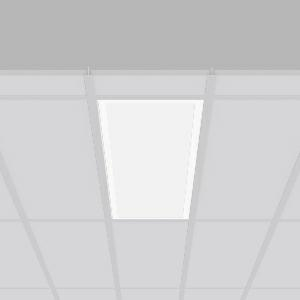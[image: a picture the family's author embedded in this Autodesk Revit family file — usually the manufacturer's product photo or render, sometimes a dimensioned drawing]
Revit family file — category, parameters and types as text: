
# Revit family: sidelite_eco_672377_002_1_5599
name_source: partatom
category: Lighting Fixtures
units: mm (PartAtom-declared; Revit-internal decimal feet)

## family parameters
Cut with Voids When Loaded = No
Host = Face
Light Source = No
Part Type = Normal
Room Calculation Point = No
Round Connector Dimension = Use Diameter
Shared = No

## types (1)
- SIDELITE ECO (1 x LED Modul 840, 3500 lm, 4000)
    Apparent Load = 29 VA
    CIE Flux Codes = 47 79 96 100 100
    Color Rendering = 80
    Color Temperature = 4000
    Default Elevation = 1800 mm
    Description = Series: SIDELITE ECO
Highly economical recessed luminaire with progressive LED technology. For escape route illumination. Frame made of aluminium, powder-coated. Diffuser: plastic, opal. Lightguide and diffuser made of non-yellowing plastic (PMMA). Lateral light emission (RZB SIDELITE technology) for homogeneous light distribution. External driver. Self-contained system with automatic self-test. External driver with simple plug-in locking system. Extended connection cable (1.90 m). 
Colour: white
Length: 1245 mm
Width: 308 mm
Cut-out length: 1220 mm
Cut-out width: 285 mm
Recess height: 160 mm
Luminaire: recess height: 40 mm
Weight: 4.7 kg
Operating mode: maintained power mode
Duration time: 3 h
Lamp: LED
Socket: without socket
Colour temperature: 4000K
Colour rendering index (CRI): 80
System power: 29 W
Rated luminous flux: 3500 lm
Luminous flux, emergency: 520 lm
System power, emergency: -
Control gear: Regulated power supply
Protection class: I
Type of protection: IP 40
    Height = 0 mm  [stored 0 ft]
    Lamp = 1 x LED Modul 840
    Lamp Light Flux = 3500 lm
    Lamp count = 1
    Length = 1245 mm
    Lifetime = 50000 h
    Luminous efficacy = 121 lm/W
    Manufacturer = RZB
    ModVariant = No
    Model = 672377.002.1
    Mounting Place = Ceiling
    Mounting Type = Recessed
    Number of Poles = 1
    OnlyDefault = Yes
    Power Factor = 1
    Product Name = SIDELITE ECO
    Product group = Recessed modular luminaires
    ProductGroupID = 406
    Protection Class = Protection class I
    Protection Degree = IP 40
    RLX_Detail_Level = 1
    RLX_Emergency_Light_Flux = 520 lm
    RLX_Emergency_Type = 3
    RLX_Emergency_Type_DB = Yes
    RlxData = <blob elided: 29941 chars, md5=04672c4c>
    Socket = socket
    Standby Power = 0 W
    System Light Flux = 3500 lm
    System Power = 29 W
    Type Comments = Product without accessories
    Type Image = 312367.002.jpg
    URL = http://relux.com
    VarID = ---
    Voltage = 230 V
    Voltage Range = 220-240 V
    Weight = 0.00 kg
    Width = 308 mm

note: [stored X ft] marks values corroborated as IEEE doubles in the binary element streams (Revit-internal decimal feet)

## geometry (parser evidence)
native form markers: Blend x4, Sweep x11
no freeform markers — native parametric forms only
